FCSTD DOCUMENT  (FreeCAD 0.21R33668 +26 (Git))
Label: forme 2
License: All rights reserved
LicenseURL: http://en.wikipedia.org/wiki/All_rights_reserved
objects: Part::Feature×6, Part::RegularPolygon×2, Part::Circle×1, Part::Vertex×1
note: 10 computed .brp shape members not serialized (recipe doc carries the construction recipe); baked Part::Feature solids carry a one-line shape summary decoded from their .brp

FEATURE [Part::Circle] Circle  label="Cercle"
  Angle1 = 0
  Angle2 = 360
  AttacherType = Attacher::AttachEngine3D
  Radius = 20
FEATURE [Part::RegularPolygon] RegularPolygon  label="Polygone régulier"
  AttacherType = Attacher::AttachEngine3D
  Circumradius = 12
  Polygon = 6
FEATURE [Part::RegularPolygon] RegularPolygon001  label="Polygone régulier001"
  AttacherType = Attacher::AttachEngine3D
  Circumradius = 8
  Polygon = 6
FEATURE [Part::Vertex] Vertex  label="Sommet"
  AttacherType = Attacher::AttachEngine3D
  X = 0
  Y = 0
  Z = 0
FEATURE [Part::Feature] Edge
  shape: bbox 2 x 3.464 x 2e-07 mm, 0 faces, 0 solids (baked)
FEATURE [Part::Feature] Edge001
  shape: bbox 4 x 2e-07 x 2e-07 mm, 0 faces, 0 solids (baked)
FEATURE [Part::Feature] Edge002
  shape: bbox 2 x 3.464 x 2e-07 mm, 0 faces, 0 solids (baked)
FEATURE [Part::Feature] Edge003
  shape: bbox 4 x 2e-07 x 2e-07 mm, 0 faces, 0 solids (baked)
FEATURE [Part::Feature] Edge004
  shape: bbox 2 x 3.464 x 2e-07 mm, 0 faces, 0 solids (baked)
FEATURE [Part::Feature] Edge005
  shape: bbox 2 x 3.464 x 2e-07 mm, 0 faces, 0 solids (baked)
